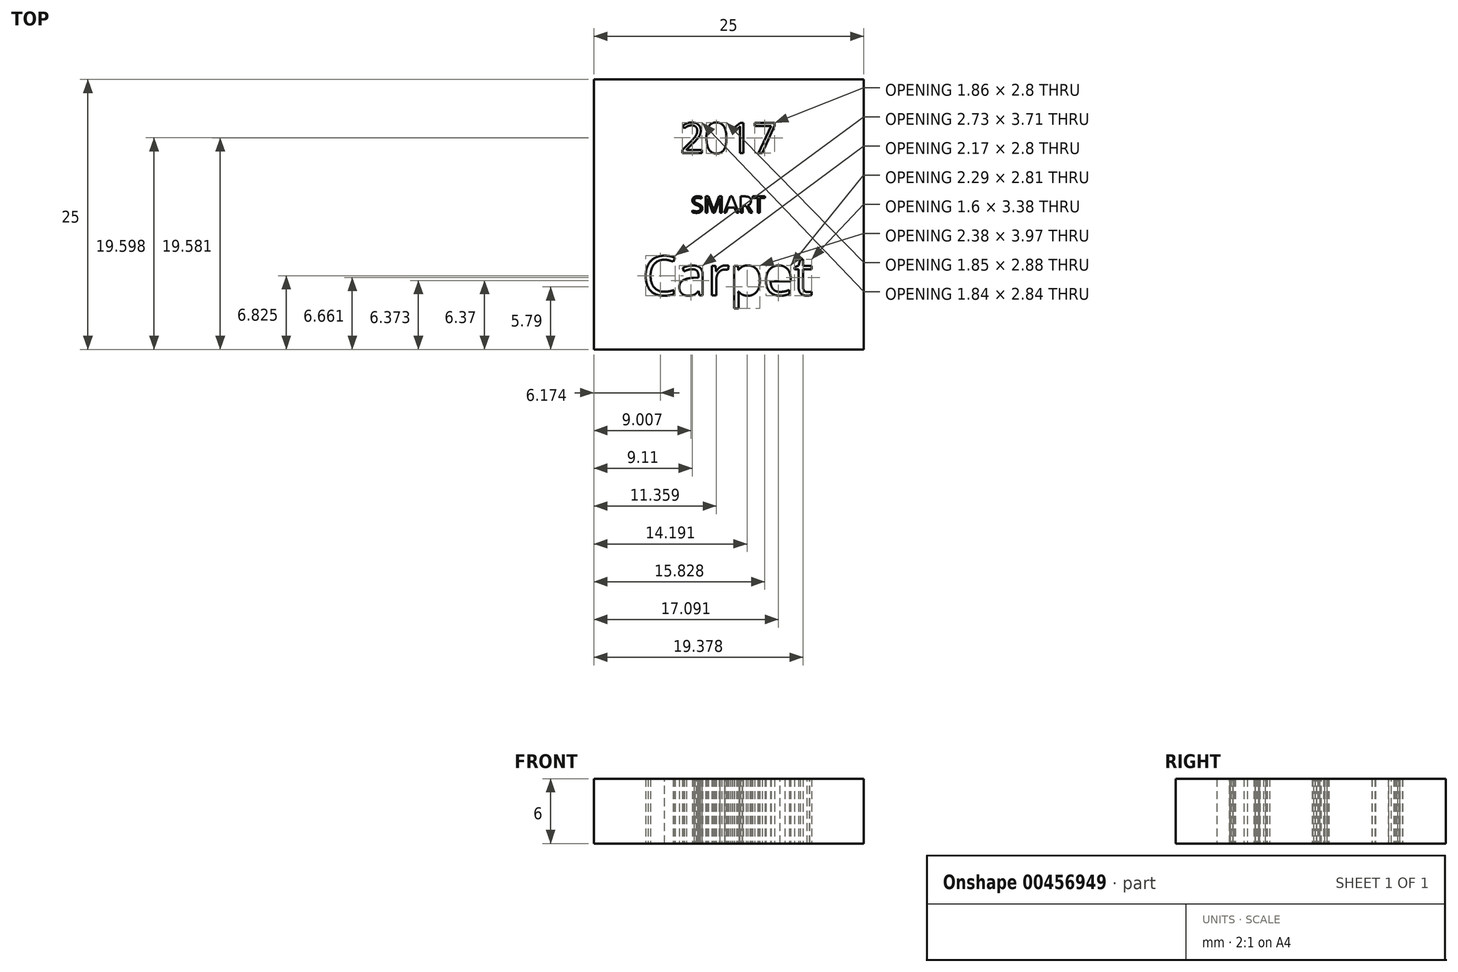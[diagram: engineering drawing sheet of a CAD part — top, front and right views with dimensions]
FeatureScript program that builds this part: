
annotation { "Feature Type Name" : "Feature", "Feature Type Description" : "" }
export const myFeature = defineFeature(function(context is Context, id is Id, definition is map)
    precondition{}
    {
        {
            var Q0;
            Q0=qCreatedBy(makeId("Top.planeOp"),FACE);
            var sketch = newSketch(context, id + "F0", { "sketchPlane" : qUnion([Q0])});
            skPoint(sketch, "E0.middle", {"position": v(0, 0) * mm});
            skLineSegment(sketch, "E1.bottom", {"start": v(12.5, 12.5) * mm, "end": v(-12.5, 12.5) * mm});
            skLineSegment(sketch, "E1.top", {"start": v(12.5, -12.5) * mm, "end": v(-12.5, -12.5) * mm});
            skLineSegment(sketch, "E1.left", {"start": v(12.5, 12.5) * mm, "end": v(12.5, -12.5) * mm});
            skLineSegment(sketch, "E1.right", {"start": v(-12.5, 12.5) * mm, "end": v(-12.5, -12.5) * mm});
            skText(sketch, "E2", { "text": "2017", "fontName": "OpenSans-Regular.ttf"});
            skText(sketch, "E3", { "text": "SMART", "fontName": "OpenSans-Regular.ttf"});
            skText(sketch, "E4", { "text": "Carpet", "fontName": "OpenSans-Regular.ttf"});
            const initialGuessF0  = {"E2": [-0.0045, 0.00568, 1, 0, 0.00282], "E3": [-0.0035, 0.00016, 1, 0, 0.00152], "E4": [-0.008, -0.00748, 1, 0, 0.00364]};
            skSetInitialGuess(sketch, initialGuessF0);
            skSolve(sketch);
        }
        {
            var Q0;
            Q0=qSketchRegion(id+"F0",true);
            extrude(context, id + "F1", {"entities" : qUnion([Q0]), "depth" : 6 * mm});
        }
    });
